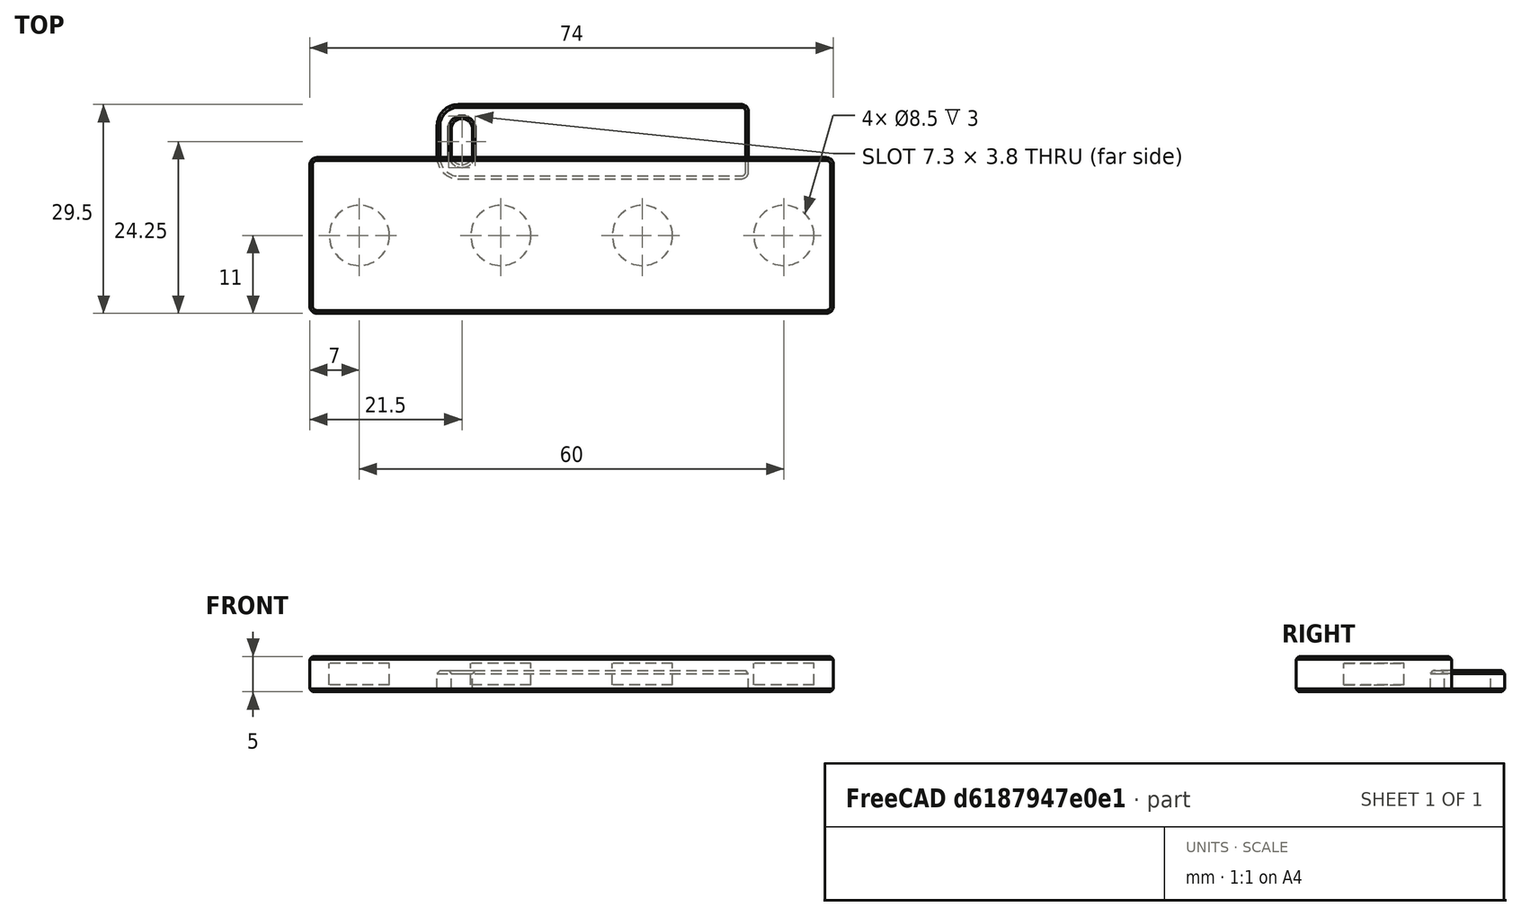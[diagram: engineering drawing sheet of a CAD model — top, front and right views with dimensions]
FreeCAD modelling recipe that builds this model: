
FCSTD DOCUMENT  (FreeCAD 0.18R16146 (Git))
Label: sanyu-magnet
License: All rights reserved
LicenseURL: http://en.wikipedia.org/wiki/All_rights_reserved
objects: Part::Cylinder×6, Part::Feature×4, Part::Box×3, Part::Fillet×3, Mesh::Feature×2, Part::MultiFuse×2, Part::Chamfer×2, Part::Cut×2
note: 22 computed .brp shape members not serialized (recipe doc carries the construction recipe); baked Part::Feature solids carry a one-line shape summary decoded from their .brp

FEATURE [Mesh::Feature] sanyu_logo  label="sanyu-logo"
FEATURE [Part::Box] Box  label="Cube"
  AttacherType = Attacher::AttachEngine3D
  Height = 5
  Length = 74
  Placement = pos=(-45,-9,0) rot=(0,0,1;0rad)
  Width = 22
FEATURE [Part::Feature] sanyu_logo001
  shape: bbox 72 x 20 x 3 mm, 7584 faces, 0 solids (baked)
FEATURE [Part::Feature] sanyu_logo001001  label="sanyu_logo002"
  Placement = pos=(0,0,4) rot=(0,0,1;0rad)
  shape: bbox 72 x 20 x 3 mm, 1576 faces, 0 solids (baked)
FEATURE [Part::Cylinder] Cylinder
  Angle = 360
  AttacherType = Attacher::AttachEngine3D
  Height = 3
  Placement = pos=(-38,2,0) rot=(0,0,1;0rad)
  Radius = 4.25
FEATURE [Part::Cylinder] Cylinder001
  Angle = 360
  AttacherType = Attacher::AttachEngine3D
  Height = 3
  Placement = pos=(22,2,0) rot=(0,0,1;0rad)
  Radius = 4.25
FEATURE [Part::Cylinder] Cylinder002
  Angle = 360
  AttacherType = Attacher::AttachEngine3D
  Height = 3
  Placement = pos=(2,2,0) rot=(0,0,1;0rad)
  Radius = 4.25
FEATURE [Part::Cylinder] Cylinder003
  Angle = 360
  AttacherType = Attacher::AttachEngine3D
  Height = 3
  Placement = pos=(-18,2,0) rot=(0,0,1;0rad)
  Radius = 4.25
FEATURE [Part::MultiFuse] Fusion
  Placement = pos=(0,0,1) rot=(0,0,1;0rad)
  Shapes = -> [Cylinder003,Cylinder001,Cylinder,Cylinder002]
FEATURE [Part::Fillet] Fillet
  Base = -> Box
  Edges = 4 edges r=1: [Edge1,Edge3,Edge5,Edge7]
FEATURE [Part::Chamfer] Chamfer
  Base = -> Fillet
  Edges = 16 edges r=0.4: [Edge1,Edge4,Edge5,Edge6,Edge7,Edge8,Edge9,Edge10,Edge11,Edge12,Edge14,Edge16,Edge17,Edge18,Edge19,Edge20]
FEATURE [Part::Cut] Cut
  Base = -> Chamfer
  Tool = -> Fusion
FEATURE [Part::Box] Box001  label="Cube001"
  AttacherType = Attacher::AttachEngine3D
  Height = 3
  Length = 44
  Placement = pos=(-27,10,0) rot=(0,0,1;0rad)
  Width = 10.5
FEATURE [Part::Cylinder] Cylinder004
  Angle = 360
  AttacherType = Attacher::AttachEngine3D
  Height = 10
  Placement = pos=(-22.5,17,0) rot=(0,0,1;0rad)
  Radius = 1.5
FEATURE [Part::Cylinder] Cylinder005
  Angle = 360
  AttacherType = Attacher::AttachEngine3D
  Height = 10
  Placement = pos=(-22.5,13.5,0) rot=(0,0,1;0rad)
  Radius = 1.5
FEATURE [Part::Box] Box002  label="Cube002"
  AttacherType = Attacher::AttachEngine3D
  Height = 10
  Length = 3
  Placement = pos=(-24,13.5,0) rot=(0,0,1;0rad)
  Width = 3.5
FEATURE [Part::MultiFuse] Fusion001
  Placement = pos=(-1,0,0) rot=(0,0,1;0rad)
  Shapes = -> [Cylinder004,Box002,Cylinder005]
FEATURE [Mesh::Feature] sanyu_logo_2_  label="sanyu-logo(2)"
FEATURE [Part::Feature] sanyu_logo_2_001
  shape: bbox 37 x 9 x 1.998 mm, 1790 faces, 0 solids (baked)
FEATURE [Part::Feature] sanyu_logo_2_001001  label="sanyu_logo_2_002"
  Placement = pos=(0,0,2) rot=(0,0,1;0rad)
  shape: bbox 37 x 9 x 1.998 mm, 453 faces, 0 solids (baked)
FEATURE [Part::Cut] Cut001
  Base = -> Box001
  Tool = -> Fusion001
FEATURE [Part::Fillet] Fillet001
  Base = -> Cut001
  Edges = 2 edges r=1: [Edge6,Edge15]
FEATURE [Part::Fillet] Fillet002
  Base = -> Fillet001
  Edges = 2 edges r=3: [Edge3,Edge17]
FEATURE [Part::Chamfer] Chamfer001
  Base = -> Fillet002
  Edges = 24 edges r=0.4: [Edge1,Edge4,Edge5,Edge6,Edge7,Edge8,Edge9,Edge10,Edge11,Edge12,Edge13,Edge14,Edge15,Edge17,Edge19,Edge20,Edge21,Edge22,Edge23,Edge24,Edge25,Edge26,Edge27,Edge28]
